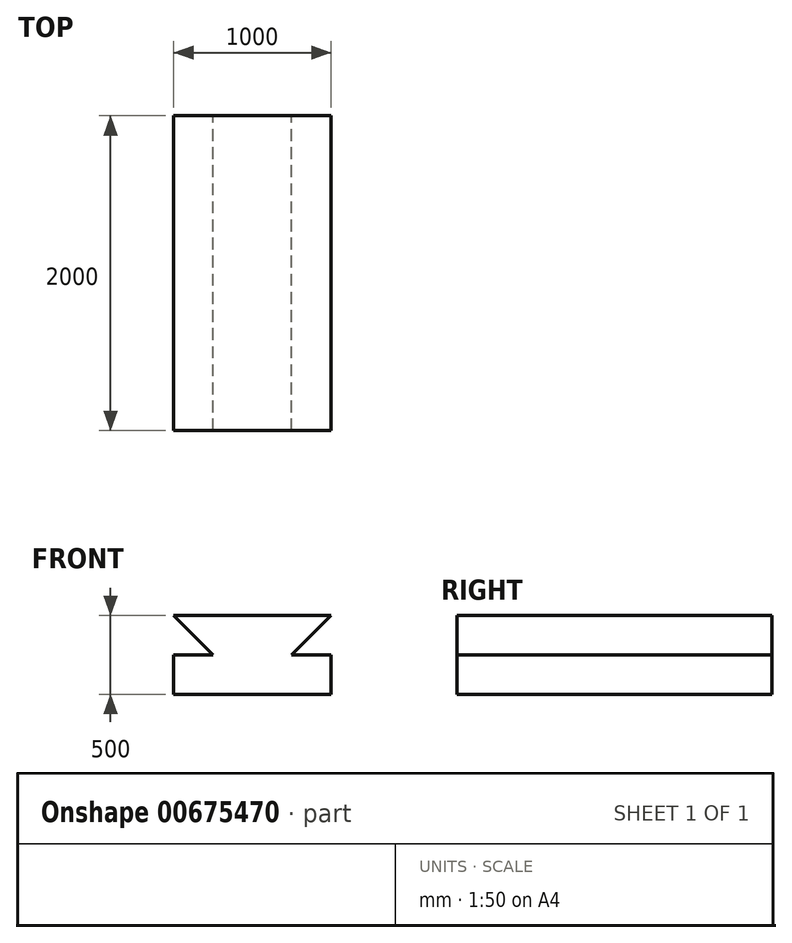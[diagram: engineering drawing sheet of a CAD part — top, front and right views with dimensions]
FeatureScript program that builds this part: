
annotation { "Feature Type Name" : "Feature", "Feature Type Description" : "" }
export const myFeature = defineFeature(function(context is Context, id is Id, definition is map)
    precondition{}
    {
        {
            var Q0;
            Q0=qCreatedBy(makeId("Front.planeOp"),FACE);
            var sketch = newSketch(context, id + "F0", { "sketchPlane" : qUnion([Q0])});
            skLineSegment(sketch, "E0", {"start": v(0, 0) * mm, "end": v(-1000, 0) * mm});
            skLineSegment(sketch, "E1", {"start": v(-1000, 0) * mm, "end": v(-1000, 250) * mm});
            skLineSegment(sketch, "E2", {"start": v(-1000, 250) * mm, "end": v(-750, 250) * mm});
            skLineSegment(sketch, "E3", {"start": v(-750, 250) * mm, "end": v(-1000, 500) * mm});
            skLineSegment(sketch, "E4", {"start": v(-1000, 500) * mm, "end": v(0, 500) * mm});
            skLineSegment(sketch, "E5", {"start": v(0, 0) * mm, "end": v(0, 250) * mm});
            skLineSegment(sketch, "E6", {"start": v(0, 250) * mm, "end": v(-250, 250) * mm});
            skLineSegment(sketch, "E7", {"start": v(-250, 250) * mm, "end": v(0, 500) * mm});
            skSolve(sketch);
        }
        {
            var Q0;
            Q0 = qSketchRegion(id + "F0", true);
            extrude(context, id + "F1", {"entities" : qUnion([Q0]), "depth" : 2000 * mm, "offsetDistance" : 25 * mm});
        }
    });
